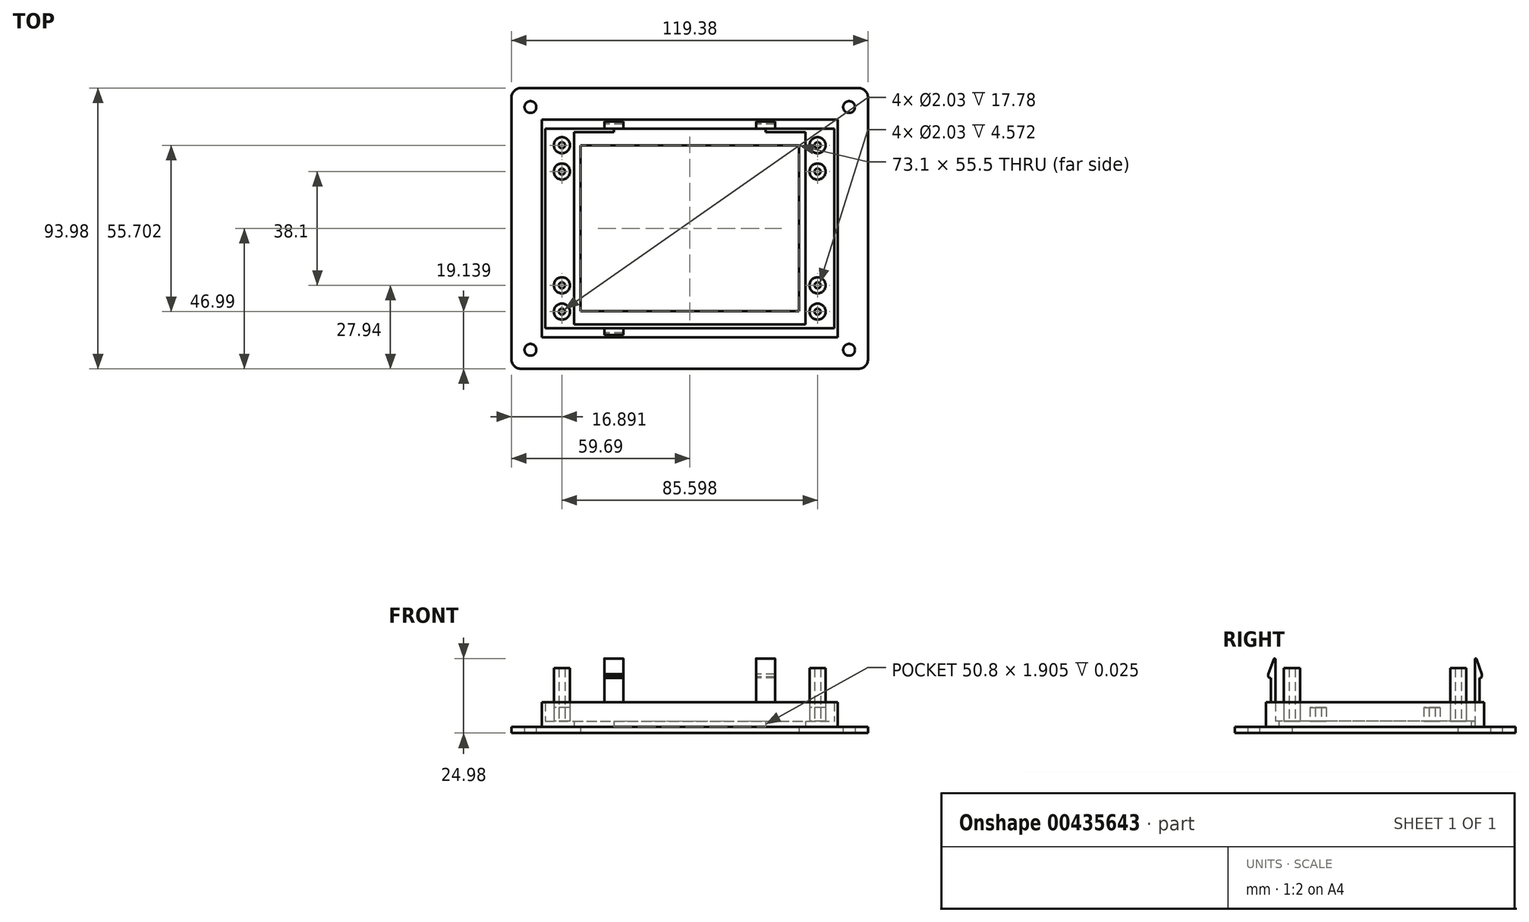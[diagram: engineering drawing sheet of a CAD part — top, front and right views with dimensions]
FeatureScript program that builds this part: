
annotation { "Feature Type Name" : "Feature", "Feature Type Description" : "" }
export const myFeature = defineFeature(function(context is Context, id is Id, definition is map)
    precondition{}
    {
        {
            var Q0;
            Q0=qCreatedBy(makeId("Top.planeOp"),FACE);
            var sketch = newSketch(context, id + "F0", { "sketchPlane" : qUnion([Q0])});
            skLineSegment(sketch, "E0.bottom", {"start": v(-56.52, 47) * mm, "end": v(56.52, 47) * mm});
            skLineSegment(sketch, "E0.top", {"start": v(-56.52, -47) * mm, "end": v(56.52, -47) * mm});
            skLineSegment(sketch, "E0.left", {"start": v(-59.69, 43.82) * mm, "end": v(-59.7, -43.82) * mm});
            skLineSegment(sketch, "E0.right", {"start": v(59.7, 43.82) * mm, "end": v(59.69, -43.82) * mm});
            skLineSegment(sketch, "E1", {"start": v(-59.7, 47) * mm, "end": v(59.7, -47) * mm, "construction": true});
            skLineSegment(sketch, "E2", {"start": v(-59.7, -47) * mm, "end": v(59.7, 47) * mm, "construction": true});
            skCircle(sketch, "E3", {"center": v(-53.34, 40.64) * mm, "radius": 1.98 * mm});
            skCircle(sketch, "E4.MirrorC", {"center": v(53.34, 40.64) * mm, "radius": 1.98 * mm});
            skCircle(sketch, "E5.MirrorC", {"center": v(-53.34, -40.64) * mm, "radius": 1.98 * mm});
            skCircle(sketch, "E6.MirrorC", {"center": v(53.34, -40.64) * mm, "radius": 1.98 * mm});
            skPoint(sketch, "E7.visualSharp", {"position": v(-59.69, 47) * mm});
            skArc(sketch, "E7.filletArc", {"start": v(-56.52, 47) * mm, "mid": v(-58.76, 46.06) * mm, "end": v(-59.69, 43.82) * mm});
            skPoint(sketch, "E8.visualSharp", {"position": v(59.7, 47) * mm});
            skArc(sketch, "E8.filletArc", {"start": v(59.7, 43.82) * mm, "mid": v(58.76, 46.06) * mm, "end": v(56.52, 46.99) * mm});
            skPoint(sketch, "E9.visualSharp", {"position": v(59.69, -47) * mm});
            skArc(sketch, "E9.filletArc", {"start": v(56.52, -47) * mm, "mid": v(58.76, -46.06) * mm, "end": v(59.7, -43.82) * mm});
            skPoint(sketch, "E10.visualSharp", {"position": v(-59.7, -47) * mm});
            skArc(sketch, "E10.filletArc", {"start": v(-59.7, -43.82) * mm, "mid": v(-58.76, -46.06) * mm, "end": v(-56.52, -47) * mm});
            skLineSegment(sketch, "E11.bottom", {"start": v(-36.55, 27.75) * mm, "end": v(36.55, 27.75) * mm});
            skLineSegment(sketch, "E11.top", {"start": v(-36.55, -27.75) * mm, "end": v(36.55, -27.75) * mm});
            skLineSegment(sketch, "E11.left", {"start": v(-36.55, 27.75) * mm, "end": v(-36.55, -27.75) * mm});
            skLineSegment(sketch, "E11.right", {"start": v(36.55, 27.75) * mm, "end": v(36.55, -27.75) * mm});
            skLineSegment(sketch, "E12", {"start": v(-36.55, 27.75) * mm, "end": v(36.55, -27.75) * mm, "construction": true});
            skLineSegment(sketch, "E13", {"start": v(-36.55, -27.75) * mm, "end": v(36.55, 27.75) * mm, "construction": true});
            skSolve(sketch);
        }
        {
            var Q0;
            Q0 = qSketchRegion(id + "F0", true);
            extrude(context, id + "F1", {"entities" : qUnion([Q0]), "depth" : 2.03 * mm});
        }
        {
            var Q0;
            Q0=makeQuery(id+"F1.opExtrude","CAP_FACE",FACE,{"disambiguationData":[OSD([sQuery(id+"F0.wireOp",EDGE,"E0.bottom"),sQuery(id+"F0.wireOp",EDGE,"E0.top"),sQuery(id+"F0.wireOp",EDGE,"E0.left"),sQuery(id+"F0.wireOp",EDGE,"E0.right"),sQuery(id+"F0.wireOp",EDGE,"E3"),sQuery(id+"F0.wireOp",EDGE,"E4.MirrorC"),sQuery(id+"F0.wireOp",EDGE,"E5.MirrorC"),sQuery(id+"F0.wireOp",EDGE,"E6.MirrorC"),sQuery(id+"F0.wireOp",EDGE,"E7.filletArc"),sQuery(id+"F0.wireOp",EDGE,"E8.filletArc"),sQuery(id+"F0.wireOp",EDGE,"E9.filletArc"),sQuery(id+"F0.wireOp",EDGE,"E10.filletArc"),sQuery(id+"F0.wireOp",EDGE,"E11.bottom"),sQuery(id+"F0.wireOp",EDGE,"E11.top"),sQuery(id+"F0.wireOp",EDGE,"E11.left"),sQuery(id+"F0.wireOp",EDGE,"E11.right")])],"isStart":false});
            var sketch = newSketch(context, id + "F2", { "sketchPlane" : qUnion([Q0])});
            skLineSegment(sketch, "E14.bottom", {"start": v(-49.53, 36.49) * mm, "end": v(49.53, 36.49) * mm});
            skLineSegment(sketch, "E14.top", {"start": v(-49.53, -36.49) * mm, "end": v(49.53, -36.49) * mm});
            skLineSegment(sketch, "E14.left", {"start": v(-49.53, 36.49) * mm, "end": v(-49.53, -36.49) * mm});
            skLineSegment(sketch, "E14.right", {"start": v(49.53, 36.49) * mm, "end": v(49.53, -36.49) * mm});
            skLineSegment(sketch, "E15", {"start": v(-49.53, 36.49) * mm, "end": v(49.53, -36.49) * mm, "construction": true});
            skLineSegment(sketch, "E16", {"start": v(-49.53, -36.49) * mm, "end": v(49.53, 36.49) * mm, "construction": true});
            skLineSegment(sketch, "E17.top", {"start": v(-38.68, -32.18) * mm, "end": v(38.68, -32.18) * mm});
            skLineSegment(sketch, "E17.left", {"start": v(-38.68, 32.18) * mm, "end": v(-38.68, -32.18) * mm});
            skLineSegment(sketch, "E17.right", {"start": v(38.68, 32.18) * mm, "end": v(38.68, -32.18) * mm});
            skLineSegment(sketch, "E18", {"start": v(-38.68, 32.18) * mm, "end": v(-25.42, 32.18) * mm});
            skLineSegment(sketch, "E19", {"start": v(-25.42, 32.18) * mm, "end": v(-25.42, 33.45) * mm});
            skLineSegment(sketch, "E20", {"start": v(-25.42, 33.45) * mm, "end": v(25.38, 33.45) * mm});
            skLineSegment(sketch, "E21", {"start": v(25.38, 33.45) * mm, "end": v(25.38, 32.18) * mm});
            skLineSegment(sketch, "E22", {"start": v(25.38, 32.18) * mm, "end": v(38.68, 32.18) * mm});
            skLineSegment(sketch, "E23", {"start": v(-38.68, 32.18) * mm, "end": v(38.68, -32.18) * mm, "construction": true});
            skLineSegment(sketch, "E24", {"start": v(-38.68, -32.18) * mm, "end": v(38.68, 32.18) * mm, "construction": true});
            skSolve(sketch);
        }
        {
            var Q0;
            Q0 = qSketchRegion(id + "F2", true);
            extrude(context, id + "F3", {"entities" : qUnion([Q0]), "operationType" : NewBodyOperationType.ADD, "depth" : 1.9 * mm});
        }
        {
            var Q0;
            Q0=makeQuery(id+"F3.opExtrude","CAP_FACE",FACE,{"disambiguationData":[OSD([sQuery(id+"F2.wireOp",EDGE,"E14.bottom"),sQuery(id+"F2.wireOp",EDGE,"E14.top"),sQuery(id+"F2.wireOp",EDGE,"E14.left"),sQuery(id+"F2.wireOp",EDGE,"E14.right"),sQuery(id+"F2.wireOp",EDGE,"E17.top"),sQuery(id+"F2.wireOp",EDGE,"E17.left"),sQuery(id+"F2.wireOp",EDGE,"E17.right"),sQuery(id+"F2.wireOp",EDGE,"E18"),sQuery(id+"F2.wireOp",EDGE,"E19"),sQuery(id+"F2.wireOp",EDGE,"E20"),sQuery(id+"F2.wireOp",EDGE,"E21"),sQuery(id+"F2.wireOp",EDGE,"E22")])],"isStart":false});
            var sketch = newSketch(context, id + "F4", { "sketchPlane" : qUnion([Q0])});
            skLineSegment(sketch, "E25", {"start": v(-49.53, 36.49) * mm, "end": v(-49.53, -36.49) * mm});
            skLineSegment(sketch, "E26", {"start": v(-49.53, -36.49) * mm, "end": v(49.53, -36.49) * mm});
            skLineSegment(sketch, "E27", {"start": v(49.53, -36.49) * mm, "end": v(49.53, 36.49) * mm});
            skLineSegment(sketch, "E28", {"start": v(49.53, 36.49) * mm, "end": v(-49.53, 36.49) * mm});
            skLineSegment(sketch, "E29.bottom", {"start": v(-48.39, 33.43) * mm, "end": v(48.39, 33.43) * mm});
            skLineSegment(sketch, "E29.top", {"start": v(-48.39, -33.43) * mm, "end": v(48.39, -33.43) * mm});
            skLineSegment(sketch, "E29.left", {"start": v(-48.39, 33.43) * mm, "end": v(-48.39, -33.43) * mm});
            skLineSegment(sketch, "E29.right", {"start": v(48.39, 33.43) * mm, "end": v(48.39, -33.43) * mm});
            skLineSegment(sketch, "E30", {"start": v(-48.39, 33.43) * mm, "end": v(48.39, -33.43) * mm, "construction": true});
            skLineSegment(sketch, "E31", {"start": v(-48.39, -33.43) * mm, "end": v(48.39, 33.43) * mm, "construction": true});
            skSolve(sketch);
        }
        {
            var Q0;
            Q0 = qSketchRegion(id + "F4", true);
            extrude(context, id + "F5", {"entities" : qUnion([Q0]), "operationType" : NewBodyOperationType.ADD, "depth" : 6.35 * mm});
        }
        {
            var Q0;
            Q0=makeQuery(id+"F3.opExtrude","CAP_FACE",FACE,{"disambiguationData":[OSD([sQuery(id+"F2.wireOp",EDGE,"E14.bottom"),sQuery(id+"F2.wireOp",EDGE,"E14.top"),sQuery(id+"F2.wireOp",EDGE,"E14.left"),sQuery(id+"F2.wireOp",EDGE,"E14.right"),sQuery(id+"F2.wireOp",EDGE,"E17.top"),sQuery(id+"F2.wireOp",EDGE,"E17.left"),sQuery(id+"F2.wireOp",EDGE,"E17.right"),sQuery(id+"F2.wireOp",EDGE,"E18"),sQuery(id+"F2.wireOp",EDGE,"E19"),sQuery(id+"F2.wireOp",EDGE,"E20"),sQuery(id+"F2.wireOp",EDGE,"E21"),sQuery(id+"F2.wireOp",EDGE,"E22")])],"isStart":false});
            var sketch = newSketch(context, id + "F6", { "sketchPlane" : qUnion([Q0])});
            skCircle(sketch, "E32", {"center": v(-42.8, 27.85) * mm, "radius": 2.7 * mm});
            skCircle(sketch, "E33", {"center": v(-42.8, 27.85) * mm, "radius": 1.02 * mm});
            skCircle(sketch, "E34", {"center": v(-42.8, -27.85) * mm, "radius": 2.7 * mm});
            skCircle(sketch, "E35", {"center": v(42.8, -27.85) * mm, "radius": 2.7 * mm});
            skCircle(sketch, "E36", {"center": v(42.8, 27.85) * mm, "radius": 2.7 * mm});
            skCircle(sketch, "E37", {"center": v(42.8, 27.85) * mm, "radius": 1.02 * mm});
            skCircle(sketch, "E38", {"center": v(42.8, -27.85) * mm, "radius": 1.02 * mm});
            skCircle(sketch, "E39", {"center": v(-42.8, -27.85) * mm, "radius": 1.02 * mm});
            skSolve(sketch);
        }
        {
            var Q0;
            Q0 = qSketchRegion(id + "F6", true);
            extrude(context, id + "F7", {"entities" : qUnion([Q0]), "operationType" : NewBodyOperationType.ADD, "depth" : 17.78 * mm});
        }
        {
            var Q0;
            {var subQ1=sQuery(id+"F2.wireOp",EDGE,"E22");var subQ3=sQuery(id+"F2.wireOp",EDGE,"E21");var subQ4=sQuery(id+"F2.wireOp",EDGE,"E19");var subQ7=sQuery(id+"F2.wireOp",EDGE,"E17.top");var subQ8=sQuery(id+"F2.wireOp",EDGE,"E17.left");var subQ9=sQuery(id+"F2.wireOp",EDGE,"E17.right");var subQ10=sQuery(id+"F2.wireOp",EDGE,"E18");Q0=makeQuery(id+"F7.boolean.opBoolean","SPLIT",FACE,{"disambiguationData":[TD([makeQuery(id+"F3.opExtrude","SWEPT_FACE",FACE,{"disambiguationData":[OSD([subQ7])]})])],"derivedFrom":makeQuery(id+"F3.opExtrude","CAP_FACE",FACE,{"disambiguationData":[OSD([sQuery(id+"F2.wireOp",EDGE,"E14.bottom"),sQuery(id+"F2.wireOp",EDGE,"E14.top"),sQuery(id+"F2.wireOp",EDGE,"E14.left"),sQuery(id+"F2.wireOp",EDGE,"E14.right"),subQ7,subQ8,subQ9,subQ10,subQ4,sQuery(id+"F2.wireOp",EDGE,"E20"),subQ3,subQ1])],"isStart":false})});}
            var sketch = newSketch(context, id + "F8", { "sketchPlane" : qUnion([Q0])});
            skCircle(sketch, "E40", {"center": v(-42.8, 19.05) * mm, "radius": 2.7 * mm});
            skCircle(sketch, "E41", {"center": v(-42.8, -19.05) * mm, "radius": 2.7 * mm});
            skCircle(sketch, "E42", {"center": v(42.8, 19.05) * mm, "radius": 2.7 * mm});
            skCircle(sketch, "E43", {"center": v(42.8, -19.05) * mm, "radius": 2.7 * mm});
            skLineSegment(sketch, "E44", {"start": v(-42.8, 27.85) * mm, "end": v(-42.8, -27.85) * mm, "construction": true});
            skLineSegment(sketch, "E45", {"start": v(42.8, 27.85) * mm, "end": v(42.8, -27.85) * mm, "construction": true});
            skCircle(sketch, "E46", {"center": v(-42.8, 19.05) * mm, "radius": 1.02 * mm});
            skCircle(sketch, "E47", {"center": v(-42.8, -19.05) * mm, "radius": 1.02 * mm});
            skCircle(sketch, "E48", {"center": v(42.8, 19.05) * mm, "radius": 1.02 * mm});
            skCircle(sketch, "E49", {"center": v(42.8, -19.05) * mm, "radius": 1.02 * mm});
            skSolve(sketch);
        }
        {
            var Q0;
            Q0 = qSketchRegion(id + "F8", true);
            extrude(context, id + "F9", {"entities" : qUnion([Q0]), "operationType" : NewBodyOperationType.ADD, "depth" : 4.57 * mm});
        }
        {
            var Q0;
            Q0=qCreatedBy(makeId("Right.planeOp"),FACE);
            cPlane(context, id + "F10", {"entities" : qUnion([Q0]), "cplaneType" : CPlaneType.OFFSET, "offset" : 25.4 * mm, "oppositeDirection" : true, "width" : 152.4 * mm, "height" : 152.4 * mm});
        }
        {
            var Q0;
            Q0=qCreatedBy(id+"F10.planeOp",FACE);
            var sketch = newSketch(context, id + "F11", { "sketchPlane" : qUnion([Q0])});
            skLineSegment(sketch, "E50", {"start": v(-33.43, 10.29) * mm, "end": v(-33.43, 24.72) * mm});
            skLineSegment(sketch, "E51", {"start": v(-35.46, 18.47) * mm, "end": v(-34.95, 18.47) * mm});
            skLineSegment(sketch, "E52", {"start": v(-34.95, 18.47) * mm, "end": v(-34.95, 10.29) * mm});
            skLineSegment(sketch, "E53", {"start": v(-34.95, 10.29) * mm, "end": v(-33.43, 10.29) * mm});
            skLineSegment(sketch, "E54", {"start": v(-35.76, 18.83) * mm, "end": v(-35.46, 18.47) * mm});
            skLineSegment(sketch, "E55", {"start": v(-35.76, 18.83) * mm, "end": v(-35.76, 19.74) * mm});
            skLineSegment(sketch, "E56", {"start": v(-35.76, 19.74) * mm, "end": v(-33.92, 24.8) * mm});
            skPoint(sketch, "E57.visualSharp", {"position": v(-33.43, 26.16) * mm});
            skArc(sketch, "E57.filletArc", {"start": v(-33.43, 24.72) * mm, "mid": v(-33.64, 24.97) * mm, "end": v(-33.92, 24.8) * mm});
            skLineSegment(sketch, "E58.MirrorCS", {"start": v(33.43, 10.29) * mm, "end": v(33.43, 24.72) * mm});
            skArc(sketch, "E59.MirrorCS", {"start": v(33.43, 24.72) * mm, "mid": v(33.64, 24.97) * mm, "end": v(33.92, 24.8) * mm});
            skLineSegment(sketch, "E60.MirrorCS", {"start": v(35.76, 19.74) * mm, "end": v(33.92, 24.8) * mm});
            skLineSegment(sketch, "E61.MirrorCS", {"start": v(35.76, 18.83) * mm, "end": v(35.76, 19.74) * mm});
            skLineSegment(sketch, "E62.MirrorCS", {"start": v(35.76, 18.83) * mm, "end": v(35.46, 18.47) * mm});
            skLineSegment(sketch, "E63.MirrorCS", {"start": v(35.46, 18.47) * mm, "end": v(34.95, 18.47) * mm});
            skLineSegment(sketch, "E64.MirrorCS", {"start": v(34.95, 18.47) * mm, "end": v(34.95, 10.29) * mm});
            skLineSegment(sketch, "E65.MirrorCS", {"start": v(34.95, 10.29) * mm, "end": v(33.43, 10.29) * mm});
            skSolve(sketch);
        }
        {
            var Q0;
            Q0 = qSketchRegion(id + "F11", true);
            extrude(context, id + "F12", {"entities" : qUnion([Q0]), "operationType" : NewBodyOperationType.ADD, "endBound" : BoundingType.SYMMETRIC, "depth" : 6.35 * mm});
        }
        {
            var Q0;
            Q0=qCreatedBy(makeId("Right.planeOp"),FACE);
            cPlane(context, id + "F13", {"entities" : qUnion([Q0]), "cplaneType" : CPlaneType.OFFSET, "offset" : 25.4 * mm, "width" : 152.4 * mm, "height" : 152.4 * mm});
        }
        {
            var Q0;
            Q0=qCreatedBy(id+"F13.planeOp",FACE);
            var sketch = newSketch(context, id + "F14", { "sketchPlane" : qUnion([Q0])});
            skArc(sketch, "E66.0", {"start": v(33.43, 24.72) * mm, "mid": v(33.64, 24.97) * mm, "end": v(33.92, 24.8) * mm});
            skLineSegment(sketch, "E67.0", {"start": v(35.76, 19.74) * mm, "end": v(33.92, 24.8) * mm});
            skLineSegment(sketch, "E68.0", {"start": v(33.43, 10.29) * mm, "end": v(33.43, 24.72) * mm});
            skLineSegment(sketch, "E69.0", {"start": v(35.76, 18.83) * mm, "end": v(35.76, 19.74) * mm});
            skLineSegment(sketch, "E70.0", {"start": v(35.46, 18.47) * mm, "end": v(34.95, 18.47) * mm});
            skLineSegment(sketch, "E71.0", {"start": v(35.76, 18.83) * mm, "end": v(35.46, 18.47) * mm});
            skLineSegment(sketch, "E72.0", {"start": v(34.95, 18.47) * mm, "end": v(34.95, 10.29) * mm});
            skLineSegment(sketch, "E73", {"start": v(33.43, 10.29) * mm, "end": v(34.95, 10.29) * mm});
            skSolve(sketch);
        }
        {
            var Q0;
            Q0 = qSketchRegion(id + "F14", true);
            extrude(context, id + "F15", {"entities" : qUnion([Q0]), "operationType" : NewBodyOperationType.ADD, "endBound" : BoundingType.SYMMETRIC, "depth" : 6.35 * mm});
        }
    });
